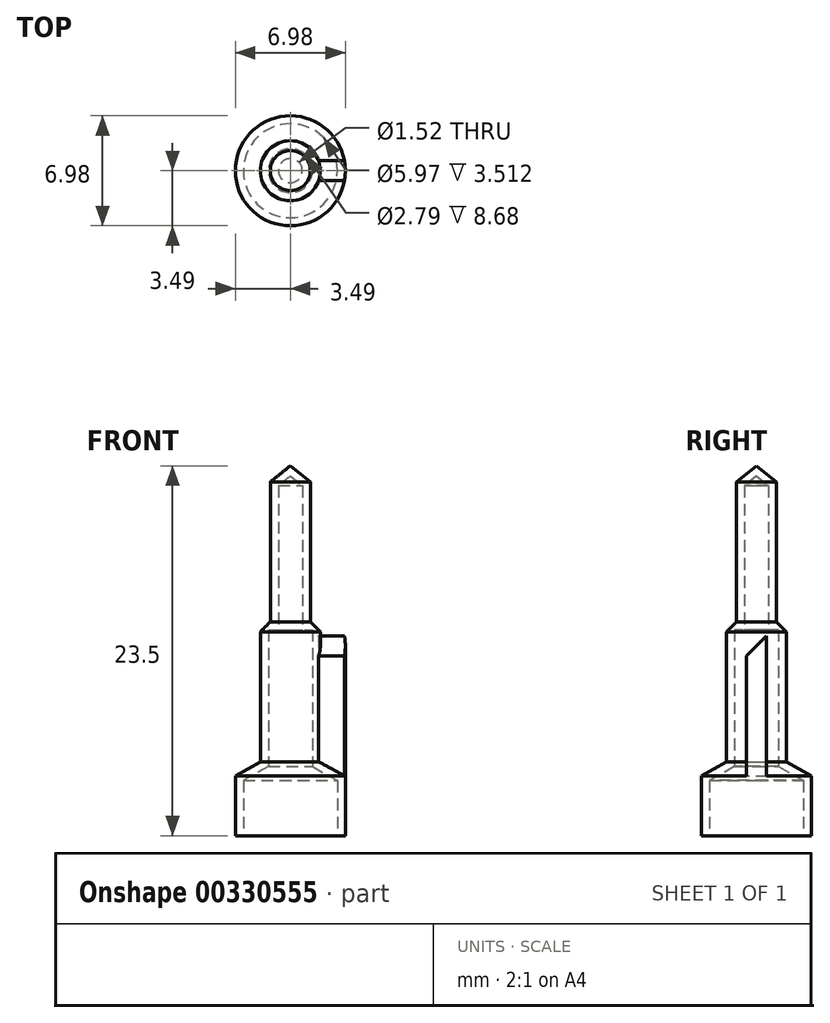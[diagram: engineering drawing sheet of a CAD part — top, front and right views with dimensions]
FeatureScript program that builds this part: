
annotation { "Feature Type Name" : "Feature", "Feature Type Description" : "" }
export const myFeature = defineFeature(function(context is Context, id is Id, definition is map)
    precondition{}
    {
        {
            var Q0;
            Q0=qCreatedBy(makeId("Front.planeOp"),FACE);
            var sketch = newSketch(context, id + "F0", { "sketchPlane" : qUnion([Q0])});
            skLineSegment(sketch, "E0", {"start": v(0, 22.84) * mm, "end": v(0, 23.5) * mm});
            skLineSegment(sketch, "E1", {"start": v(0, 23.5) * mm, "end": v(1.27, 22.48) * mm});
            skLineSegment(sketch, "E2", {"start": v(1.27, 22.48) * mm, "end": v(1.27, 13.59) * mm});
            skLineSegment(sketch, "E3", {"start": v(1.27, 13.59) * mm, "end": v(1.9, 13.59) * mm});
            skLineSegment(sketch, "E4", {"start": v(1.9, 13.59) * mm, "end": v(1.9, 4.7) * mm});
            skLineSegment(sketch, "E5", {"start": v(1.9, 4.7) * mm, "end": v(3.5, 3.8) * mm});
            skLineSegment(sketch, "E6", {"start": v(3.5, 3.81) * mm, "end": v(3.5, 0) * mm});
            skLineSegment(sketch, "E7", {"start": v(3.5, 0) * mm, "end": v(2.98, 0) * mm});
            skLineSegment(sketch, "E8.0", {"start": v(2.98, 3.51) * mm, "end": v(2.98, 0) * mm});
            skLineSegment(sketch, "E8.1", {"start": v(1.4, 4.4) * mm, "end": v(2.98, 3.51) * mm});
            skLineSegment(sketch, "E8.2", {"start": v(0, 22.84) * mm, "end": v(0.76, 22.23) * mm});
            skLineSegment(sketch, "E8.3", {"start": v(0.76, 22.23) * mm, "end": v(0.76, 13.08) * mm});
            skLineSegment(sketch, "E8.4", {"start": v(0.76, 13.08) * mm, "end": v(1.4, 13.08) * mm});
            skLineSegment(sketch, "E8.5", {"start": v(1.4, 13.08) * mm, "end": v(1.4, 4.4) * mm});
            skPoint(sketch, "E9.orphan", {"position": v(0, 0) * mm});
            skLineSegment(sketch, "E10", {"start": v(2.98, 0) * mm, "end": v(0, 0) * mm});
            skLineSegment(sketch, "E11", {"start": v(0, 22.84) * mm, "end": v(0, 0) * mm});
            skSolve(sketch);
        }
        {
            var Q0;
            Q0 = qSketchRegion(id + "F0", true);
            var Q1;
            Q1=sQuery(id+"F0.wireOp",EDGE,"E0");
            revolve(context, id + "F1", {"entities" : qUnion([Q0]), "axis" : qUnion([Q1]), "revolveType" : RevolveType.FULL});
        }
        {
            var Q0;
            Q0=qCreatedBy(makeId("Right.planeOp"),FACE);
            var sketch = newSketch(context, id + "F2", { "sketchPlane" : qUnion([Q0])});
            skLineSegment(sketch, "E12", {"start": v(0, 3.81) * mm, "end": v(-0.64, 3.81) * mm});
            skLineSegment(sketch, "E13", {"start": v(-0.64, 3.81) * mm, "end": v(-0.63, 11.43) * mm});
            skLineSegment(sketch, "E14", {"start": v(-0.63, 11.43) * mm, "end": v(0.64, 12.7) * mm});
            skLineSegment(sketch, "E15", {"start": v(0.63, 12.7) * mm, "end": v(0.63, 12.07) * mm});
            skLineSegment(sketch, "E16", {"start": v(0.63, 3.81) * mm, "end": v(0, 3.81) * mm});
            skLineSegment(sketch, "E17", {"start": v(0.64, 11.43) * mm, "end": v(0.63, 3.81) * mm});
            skLineSegment(sketch, "E18", {"start": v(0.63, 12.07) * mm, "end": v(0.63, 11.43) * mm});
            skSolve(sketch);
        }
        {
            var Q0;
            Q0 = qSketchRegion(id + "F2", true);
            var Q1;
            Q1=makeQuery(id+"F1.opRevolve","SWEPT_FACE",FACE,{"disambiguationData":[OSD([sQuery(id+"F0.wireOp",EDGE,"E6")])]});
            var Q2;
            Q2=makeQuery(id+"F1.opRevolve","SWEPT_FACE",FACE,{"disambiguationData":[OSD([sQuery(id+"F0.wireOp",EDGE,"E4")])]});
            extrude(context, id + "F3", {"entities" : qUnion([Q0]), "operationType" : NewBodyOperationType.ADD, "endBound" : BoundingType.UP_TO_SURFACE, "endBoundEntityFace" : qUnion([Q1]), "depth" : 25.4 * mm, "hasSecondDirection" : true, "secondDirectionBound" : SecondDirectionBoundingType.UP_TO_SURFACE, "secondDirectionOppositeDirection" : false, "secondDirectionBoundEntityFace" : qUnion([Q2]), "secondDirectionDepth" : 25.4 * mm});
        }
        {
            var Q0;
            Q0=makeQuery(id+"F0.imprint","IMPRINT",FACE,{"disambiguationData":[TD([[makeQuery(id+"F0.imprint","IMPRINT",EDGE,{"derivedFrom":sQuery(id+"F0.wireOp",EDGE,"E8.0")}),-1.0]])]});
            var Q1;
            Q1=sQuery(id+"F0.wireOp",EDGE,"E11");
            revolve(context, id + "F4", {"operationType" : NewBodyOperationType.REMOVE, "entities" : qUnion([Q0]), "axis" : qUnion([Q1]), "revolveType" : RevolveType.FULL, "oppositeDirection" : true});
        }
        {
            var Q0;
            Q0=makeQuery(id+"F1.opRevolve","SWEPT_EDGE",EDGE,{"disambiguationData":[OSD([sQuery(id+"F0.wireOp",EDGE,"E3"),sQuery(id+"F0.wireOp",EDGE,"E4")])]});
            chamfer(context, id + "F5", {"entities" : qUnion([Q0]), "width" : 0.64 * mm, "tangentPropagation" : true});
        }
    });
